# Revit family: Sanitary_Toilets_Sanindusa_Urby-Wall-Mounted-Toilet
name_source: partatom
category: Plumbing Fixtures
revit_build: Autodesk Revit 2018 (Build: 20170223_1515(x64)
units: mm (PartAtom-declared; Revit-internal decimal feet)

## family parameters
Always vertical = Yes
Cut with Voids When Loaded = No
Host = Wall
OmniClass Number = 23.45.00.00
OmniClass Title = Sanitary, Laundry, and Cleaning Equipment
Part Type = Normal
Room Calculation Point = No
Round Connector Dimension = Use Diameter
Shared = No

## types (1)
- SANINDUSA_WallmountedToiletwithconcealedfixation_140032004_358x480x335_Urb.y
    AssetType = Fixed
    CodePerformance = EN 997:2012 CL 1 - 6 A
    Color = White
    Constituents = Compatible toilet seats (not included): 2403100-Toilet seat urb.y clipoff with slow close system; 2401100-Toilet seat urb.y clipoff. Compatible suport frames (not inluded): 411023-SANDOUBLE free standing frame w/ dual flushing cistern for wall hung WC, 4193311-SANSLIM build-in element w/dual flushing cistern, 41733xx-SANGLASS WALL external frame w/ dual flushing cistern for wall hung WC, 40333-SANFIX frame w/ dual flushing cistern for wall hung WC, 40323-SANFIX freestanding frame w/ dual flushing cistern for wall hung WC, 40233-SANFLUSH build-in element w/ dual flushing cistern for wall hung WC, 40633-SANSPACE frame w/ dual flushing cistern for wall hung WC, 40533-SANBEST build-in element w/ dual flushing cistern for wall hung WC. 4000-Fixing kit for wall mounted toilet (included)
    Cost = 0 $
    Description = Soil appliance for the disposal of excrement.
    DrainSize = 100 mm  [stored 0.328084 ft]
    Features = Domestic and commercial use. Small wall mounted toilet, easy to clean, perfect for small spaces. It's the perfect solution for hotels.
    Finish = gloss
    InletDiameter = 50 mm  [stored 0.164042 ft]
    Installation Instructions = https://www.tec.sanindusa.pt
    InstallationDate = 1900-12-31T23:59:59
    ManufacturerName = Sanindusa
    ManufacturerURL = www.tec.sanindusa.pt
    Material = Vitreous China
    ModelNumber = 140032004
    ModelReference = Urb.y
    Name = Urb.y wall mounted toilet
    NominalHeight = 335 mm  [stored 1.09908 ft]
    NominalLength = 358 mm  [stored 1.17454 ft]
    NominalWidth = 480 mm  [stored 1.5748 ft]
    Product data url = https://www.bimobject.com
    ProductInformation = https://www.tec.sanindusa.pt
    ProductionYear = 2018
    Size = 358x480x335
    SustainabilityPerformance = n/a
n/a
    URL = www.tec.sanindusa.pt
    Uniclass2015Code = Pr_40_20_93_94
    Uniclass2015Title = WC pans
    Uniclass2015Version = Products v1.6
    Version = 1
    WarrantyDescription = https://www.tec.sanindusa.pt
    WarrantyDurationParts = 5
    WarrantyDurationUnit = year
    WarrantyStartDate = 1900-12-31T23:59:59
    Weight = 24.30 kg

note: [stored X ft] marks values corroborated as IEEE doubles in the binary element streams (Revit-internal decimal feet)

## geometry (parser evidence)
native form markers: Sweep x7
no freeform markers — native parametric forms only
